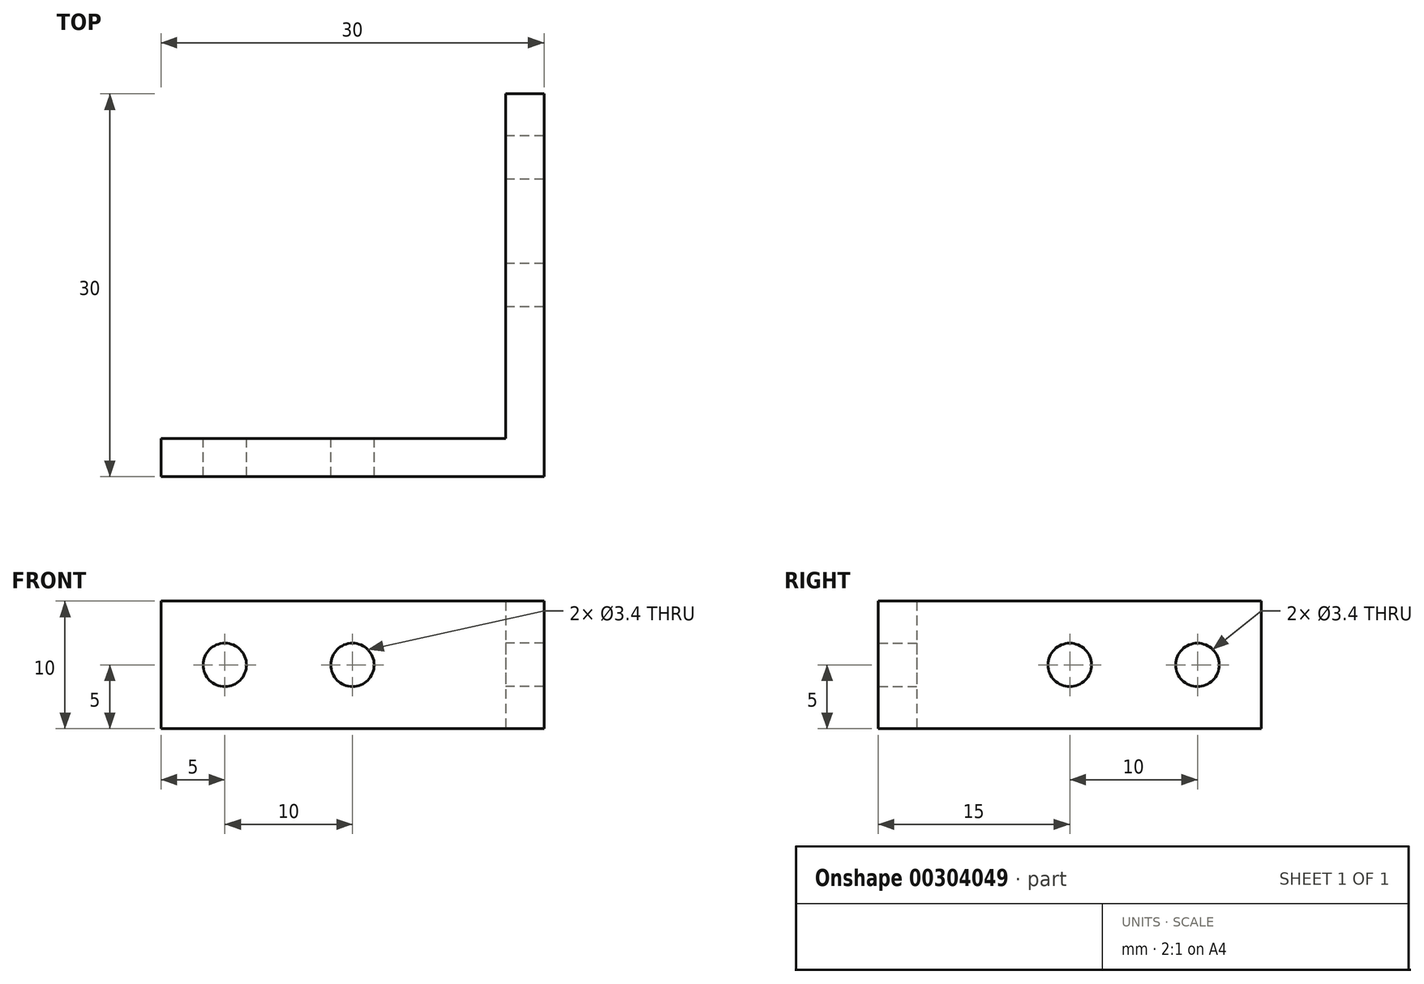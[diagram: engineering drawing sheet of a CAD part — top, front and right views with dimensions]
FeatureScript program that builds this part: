
annotation { "Feature Type Name" : "Feature", "Feature Type Description" : "" }
export const myFeature = defineFeature(function(context is Context, id is Id, definition is map)
    precondition{}
    {
        {
            var Q0;
            Q0=qCreatedBy(makeId("Top.planeOp"),FACE);
            var sketch = newSketch(context, id + "F0", { "sketchPlane" : qUnion([Q0])});
            skLineSegment(sketch, "E0", {"start": v(0, 0) * mm, "end": v(30, 0) * mm});
            skLineSegment(sketch, "E1", {"start": v(30, 0) * mm, "end": v(30, 30) * mm});
            skLineSegment(sketch, "E2", {"start": v(30, 30) * mm, "end": v(27, 30) * mm});
            skLineSegment(sketch, "E3", {"start": v(27, 30) * mm, "end": v(27, 3) * mm});
            skLineSegment(sketch, "E4", {"start": v(27, 3) * mm, "end": v(0, 3) * mm});
            skLineSegment(sketch, "E5", {"start": v(0, 3) * mm, "end": v(0, 0) * mm});
            skSolve(sketch);
        }
        {
            var Q0;
            Q0 = qSketchRegion(id + "F0", true);
            extrude(context, id + "F1", {"entities" : qUnion([Q0]), "depth" : 10 * mm});
        }
        {
            var Q0;
            Q0=makeQuery(id+"F1.opExtrude","SWEPT_FACE",FACE,{"disambiguationData":[OSD([sQuery(id+"F0.wireOp",EDGE,"E4")])]});
            var sketch = newSketch(context, id + "F2", { "sketchPlane" : qUnion([Q0])});
            skCircle(sketch, "E6", {"center": v(-5, 5) * mm, "radius": 1.7 * mm});
            skPoint(sketch, "E6.centerSnap0", {"position": v(0, 5) * mm});
            skCircle(sketch, "E7", {"center": v(-15, 5) * mm, "radius": 1.7 * mm});
            skSolve(sketch);
        }
        {
            var Q0;
            Q0=makeQuery(id+"F1.opExtrude","SWEPT_FACE",FACE,{"disambiguationData":[OSD([sQuery(id+"F0.wireOp",EDGE,"E3")])]});
            var sketch = newSketch(context, id + "F3", { "sketchPlane" : qUnion([Q0])});
            skCircle(sketch, "E8", {"center": v(-25, 5) * mm, "radius": 1.7 * mm});
            skPoint(sketch, "E8.centerSnap0", {"position": v(-30, 5) * mm});
            skCircle(sketch, "E9", {"center": v(-15, 5) * mm, "radius": 1.7 * mm});
            skSolve(sketch);
        }
        {
            var Q0;
            Q0=makeQuery(id+"F3.imprint","IMPRINT",FACE,{"disambiguationData":[TD([[makeQuery(id+"F3.imprint","IMPRINT",EDGE,{"derivedFrom":sQuery(id+"F3.wireOp",EDGE,"E8")}),1.0]])]});
            var Q1;
            Q1=makeQuery(id+"F3.imprint","IMPRINT",FACE,{"disambiguationData":[TD([[makeQuery(id+"F3.imprint","IMPRINT",EDGE,{"derivedFrom":sQuery(id+"F3.wireOp",EDGE,"E9")}),1.0]])]});
            extrude(context, id + "F4", {"entities" : qUnion([Q0, Q1]), "operationType" : NewBodyOperationType.REMOVE, "oppositeDirection" : true, "depth" : 25 * mm});
        }
        {
            var Q0;
            Q0=makeQuery(id+"F2.imprint","IMPRINT",FACE,{"disambiguationData":[TD([[makeQuery(id+"F2.imprint","IMPRINT",EDGE,{"derivedFrom":sQuery(id+"F2.wireOp",EDGE,"E7")}),1.0]])]});
            var Q1;
            Q1=makeQuery(id+"F2.imprint","IMPRINT",FACE,{"disambiguationData":[TD([[makeQuery(id+"F2.imprint","IMPRINT",EDGE,{"derivedFrom":sQuery(id+"F2.wireOp",EDGE,"E6")}),1.0]])]});
            extrude(context, id + "F5", {"entities" : qUnion([Q0, Q1]), "operationType" : NewBodyOperationType.REMOVE, "oppositeDirection" : true, "depth" : 25 * mm});
        }
    });
